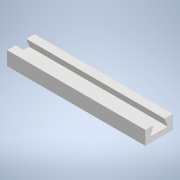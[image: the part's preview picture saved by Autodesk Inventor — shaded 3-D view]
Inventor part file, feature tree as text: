
AUTODESK INVENTOR PART (.ipt)
format: ipt  version: 2021 (Build 250183000, 183)  size: 138,752 bytes
history: native  units: mm
features: reference x12, extrude x3, sketch x3, other x2, projected_geometry x1
ambient origin geometry x8: Origin, YZ Plane, XZ Plane, XY Plane, X Axis, Y Axis, Z Axis, Center Point
bodies: Solid1 (feature_tree)
feature tree (21):
  extrude  "Extrusion1"  Depth=20.0mm
  extrude  "Extrusion2"  Depth=19.198622mm
  extrude  "Extrusion3"  Depth=6.0mm
  sketch  "Sketch1"  dims[d0=10.0mm d1=20.0mm]
  sketch  "Sketch2"  dims[d3=19.198622mm d4=19.198622mm]
  sketch  "Sketch3"  dims[d5=6.0mm d6=6.0mm d7=6.0mm d8=6.0mm d9=100.0mm d10=0.0mm d11=20.0mm d12=14.0mm d13=3.0mm d14=0.0mm d15=3.0mm d16=0.0mm]
  reference  "Reference1"
  reference  "Reference2"
  reference  "Reference3"
  reference  "Reference4"
  reference  "Reference5"
  reference  "Reference6"
  reference  "Reference7"
  projected_geometry  "Projected Loop1"
  reference  "Reference8"
  reference  "Reference9"
  reference  "Reference10"
  reference  "Reference11"
  reference  "Reference12"
  other  "Assembly1"
  other  "prismatic link outer:5"
